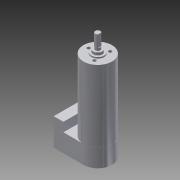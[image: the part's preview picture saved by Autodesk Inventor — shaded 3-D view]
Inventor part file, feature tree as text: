
AUTODESK INVENTOR PART (.ipt)
format: ipt  version: 2015 (Build 190159000, 159)  size: 171,520 bytes
history: native  units: mm
features: sketch x10, extrude x9, fillet x2, other x1, hole x1, pattern_circular x1
ambient origin geometry x8: Origin, YZ Plane, XZ Plane, XY Plane, X Axis, Y Axis, Z Axis, Center Point
bodies: Body1 (feature_tree)
feature tree (24):
  other  "ソリッド1"
  extrude  "押し出し1"  Depth=4.0mm
  extrude  "押し出し3"  Depth=11.0mm TaperAngle=0.0deg
  extrude  "押し出し4"  Depth=0.5mm
  extrude  "押し出し5"  Depth=9.0mm TaperAngle=0.0deg
  extrude  "押し出し6"  Depth=0.5mm
  extrude  "押し出し7"  Depth=9.0mm TaperAngle=0.0deg
  extrude  "押し出し8"  Depth=7.0mm
  fillet  "フィレット1"  Radius=2.0mm
  fillet  "フィレット2"  Radius=10.0mm
  extrude  "押し出し9"  Depth=1.0mm TaperAngle=0.0deg
  extrude  "押し出し10"  Depth=22.0mm
  hole  "穴1"  [1 undecoded]
  pattern_circular  "円形状パターン2"  [2 undecoded]
  sketch  "スケッチ1"
  sketch  "スケッチ4"
  sketch  "スケッチ5"
  sketch  "スケッチ6"
  sketch  "スケッチ7"
  sketch  "スケッチ8"
  sketch  "スケッチ10"
  sketch  "スケッチ13"
  sketch  "スケッチ14"
  sketch  "スケッチ16"
note: 3 required parameter values undecoded (feature->parameter linkage not recoverable at this tier; creation-order binding heuristic only, values carry confidence <= 0.55)
